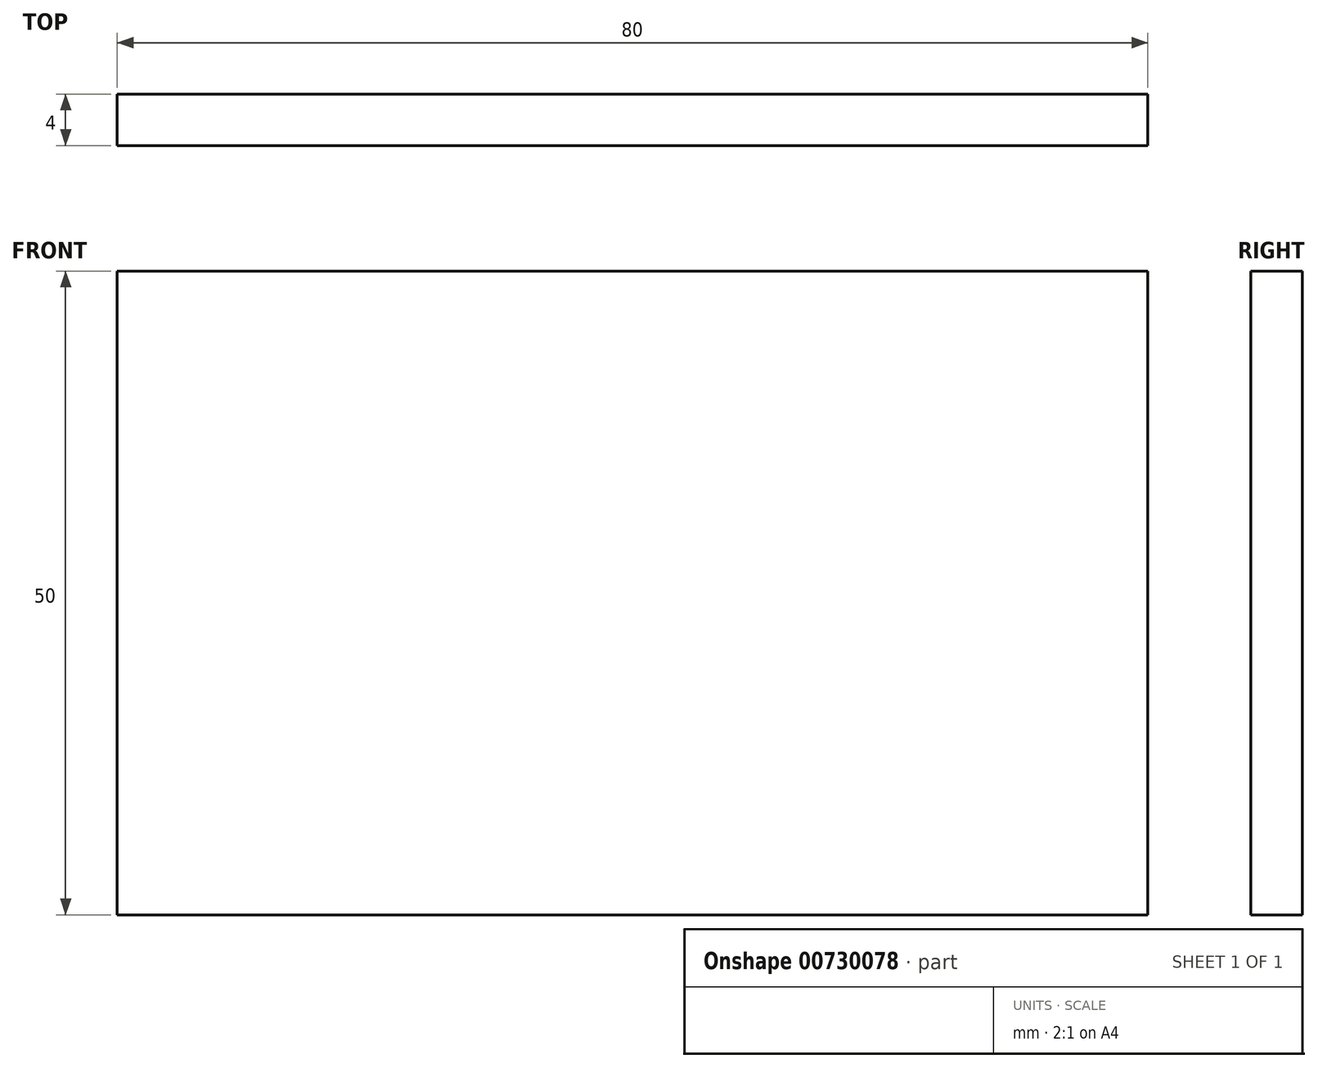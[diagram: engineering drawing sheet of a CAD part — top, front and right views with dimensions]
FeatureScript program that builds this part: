
annotation { "Feature Type Name" : "Feature", "Feature Type Description" : "" }
export const myFeature = defineFeature(function(context is Context, id is Id, definition is map)
    precondition{}
    {
        {
            var Q0;
            Q0=qCreatedBy(makeId("Top.planeOp"),FACE);
            var sketch = newSketch(context, id + "F0", { "sketchPlane" : qUnion([Q0])});
            skLineSegment(sketch, "E0.bottom", {"start": v(0, 0) * mm, "end": v(80, 0) * mm});
            skLineSegment(sketch, "E0.top", {"start": v(0, 4) * mm, "end": v(80, 4) * mm});
            skLineSegment(sketch, "E0.left", {"start": v(0, 0) * mm, "end": v(0, 4) * mm});
            skLineSegment(sketch, "E0.right", {"start": v(80, 0) * mm, "end": v(80, 4) * mm});
            skSolve(sketch);
        }
        {
            var Q0;
            Q0=makeQuery(id+"F0.imprint","IMPRINT",FACE,{"disambiguationData":[TD([[makeQuery(id+"F0.imprint","IMPRINT",EDGE,{"derivedFrom":sQuery(id+"F0.wireOp",EDGE,"E0.bottom")}),1.0]])]});
            extrude(context, id + "F1", {"entities" : qUnion([Q0]), "depth" : 50 * mm, "offsetDistance" : 25 * mm});
        }
    });
